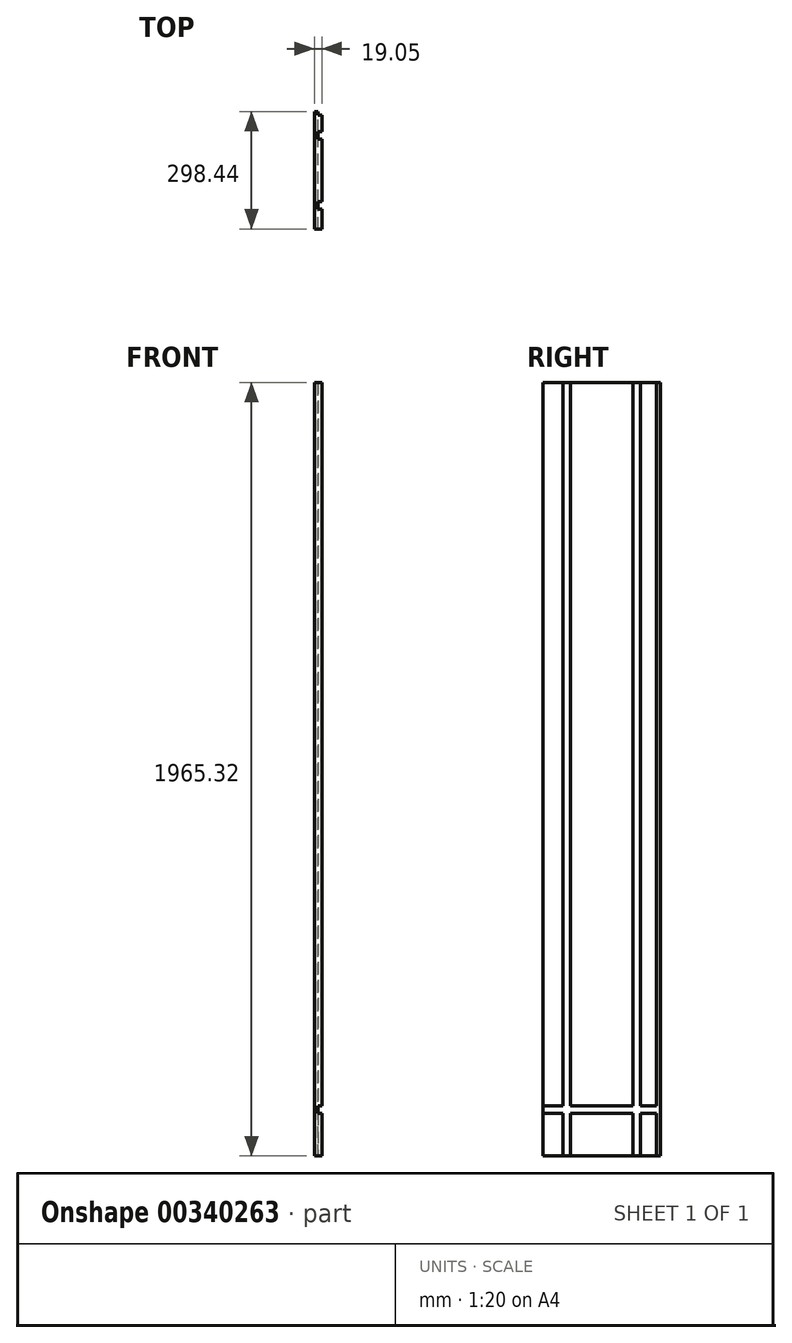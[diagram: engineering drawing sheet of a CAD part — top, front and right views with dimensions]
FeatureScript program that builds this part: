
annotation { "Feature Type Name" : "Feature", "Feature Type Description" : "" }
export const myFeature = defineFeature(function(context is Context, id is Id, definition is map)
    precondition{}
    {
        {
            var Q0;
            Q0=qCreatedBy(makeId("Right.planeOp"),FACE);
            var sketch = newSketch(context, id + "F0", { "sketchPlane" : qUnion([Q0])});
            skLineSegment(sketch, "E0.bottom", {"start": v(149.22, -982.66) * mm, "end": v(-149.23, -982.66) * mm});
            skLineSegment(sketch, "E0.top", {"start": v(149.22, 982.66) * mm, "end": v(-149.23, 982.66) * mm});
            skLineSegment(sketch, "E0.left", {"start": v(149.22, -982.66) * mm, "end": v(149.22, 982.66) * mm});
            skLineSegment(sketch, "E0.right", {"start": v(-149.23, -982.66) * mm, "end": v(-149.23, 982.66) * mm});
            skPoint(sketch, "E0.middle", {"position": v(0, 0) * mm});
            skSolve(sketch);
        }
        {
            var Q0;
            Q0=makeQuery(id+"F0.imprint","IMPRINT",FACE,{"disambiguationData":[TD([[makeQuery(id+"F0.imprint","IMPRINT",EDGE,{"derivedFrom":sQuery(id+"F0.wireOp",EDGE,"E0.bottom")}),-1.0]])]});
            extrude(context, id + "F1", {"entities" : qUnion([Q0]), "depth" : 19.05 * mm});
        }
        {
            var Q0;
            Q0=makeQuery(id+"F1.opExtrude","CAP_FACE",FACE,{"disambiguationData":[OSD([sQuery(id+"F0.wireOp",EDGE,"E0.bottom"),sQuery(id+"F0.wireOp",EDGE,"E0.top"),sQuery(id+"F0.wireOp",EDGE,"E0.left"),sQuery(id+"F0.wireOp",EDGE,"E0.right")])],"isStart":false});
            var sketch = newSketch(context, id + "F2", { "sketchPlane" : qUnion([Q0])});
            skLineSegment(sketch, "E1.bottom", {"start": v(-149.23, -855.66) * mm, "end": v(149.22, -855.66) * mm});
            skLineSegment(sketch, "E1.top", {"start": v(-149.23, -874.71) * mm, "end": v(149.22, -874.71) * mm});
            skLineSegment(sketch, "E1.left", {"start": v(-149.23, -855.66) * mm, "end": v(-149.23, -874.71) * mm});
            skLineSegment(sketch, "E1.right", {"start": v(149.22, -855.66) * mm, "end": v(149.22, -874.71) * mm});
            skSolve(sketch);
        }
        {
            var Q0;
            Q0=qSketchRegion(id+"F2",true);
            extrude(context, id + "F3", {"entities" : qUnion([Q0]), "operationType" : NewBodyOperationType.REMOVE, "oppositeDirection" : true, "depth" : 9.52 * mm});
        }
        {
            var Q0;
            {var subQ0=sQuery(id+"F0.wireOp",EDGE,"E0.top");var subQ1=sQuery(id+"F0.wireOp",EDGE,"E0.left");var subQ2=sQuery(id+"F0.wireOp",EDGE,"E0.right");Q0=makeQuery(id+"F3.boolean.opBoolean","SPLIT",FACE,{"disambiguationData":[TD([makeQuery(id+"F1.opExtrude","SWEPT_FACE",FACE,{"disambiguationData":[OSD([subQ0])]})])],"derivedFrom":makeQuery(id+"F1.opExtrude","CAP_FACE",FACE,{"disambiguationData":[OSD([sQuery(id+"F0.wireOp",EDGE,"E0.bottom"),subQ0,subQ1,subQ2])],"isStart":false})});}
            var sketch = newSketch(context, id + "F4", { "sketchPlane" : qUnion([Q0])});
            skLineSegment(sketch, "E2.bottom", {"start": v(-98.43, 982.66) * mm, "end": v(-79.38, 982.66) * mm});
            skLineSegment(sketch, "E2.top", {"start": v(-98.43, -982.66) * mm, "end": v(-79.38, -982.66) * mm});
            skLineSegment(sketch, "E2.left", {"start": v(-98.43, 982.66) * mm, "end": v(-98.43, -982.66) * mm});
            skLineSegment(sketch, "E2.right", {"start": v(-79.38, 982.66) * mm, "end": v(-79.38, -982.66) * mm});
            skLineSegment(sketch, "E3", {"start": v(0, 982.66) * mm, "end": v(0, -982.66) * mm, "construction": true});
            skLineSegment(sketch, "E4.MirrorCS", {"start": v(98.43, -982.66) * mm, "end": v(79.38, -982.66) * mm});
            skLineSegment(sketch, "E5.MirrorCS", {"start": v(98.43, 982.66) * mm, "end": v(79.38, 982.66) * mm});
            skLineSegment(sketch, "E6.MirrorCS", {"start": v(79.38, 982.66) * mm, "end": v(79.38, -982.66) * mm});
            skLineSegment(sketch, "E7.MirrorCS", {"start": v(98.43, 982.66) * mm, "end": v(98.43, -982.66) * mm});
            skSolve(sketch);
        }
        {
            var Q0;
            Q0=qSketchRegion(id+"F4",true);
            extrude(context, id + "F5", {"entities" : qUnion([Q0]), "operationType" : NewBodyOperationType.REMOVE, "oppositeDirection" : true, "depth" : 9.52 * mm});
        }
        {
            var Q0;
            Q0=makeQuery(id+"F1.opExtrude","SWEPT_FACE",FACE,{"disambiguationData":[OSD([sQuery(id+"F0.wireOp",EDGE,"E0.bottom")])]});
            var sketch = newSketch(context, id + "F6", { "sketchPlane" : qUnion([Q0])});
            skLineSegment(sketch, "E8.bottom", {"start": v(19.05, -139.7) * mm, "end": v(9.53, -139.7) * mm});
            skLineSegment(sketch, "E8.top", {"start": v(19.05, -149.22) * mm, "end": v(9.53, -149.22) * mm});
            skLineSegment(sketch, "E8.left", {"start": v(19.05, -139.7) * mm, "end": v(19.05, -149.22) * mm});
            skLineSegment(sketch, "E8.right", {"start": v(9.53, -139.7) * mm, "end": v(9.53, -149.22) * mm});
            skSolve(sketch);
        }
        {
            var Q0;
            Q0=qSketchRegion(id+"F6",true);
            extrude(context, id + "F7", {"entities" : qUnion([Q0]), "operationType" : NewBodyOperationType.REMOVE, "endBound" : BoundingType.THROUGH_ALL, "oppositeDirection" : true, "depth" : 25.4 * mm});
        }
    });
